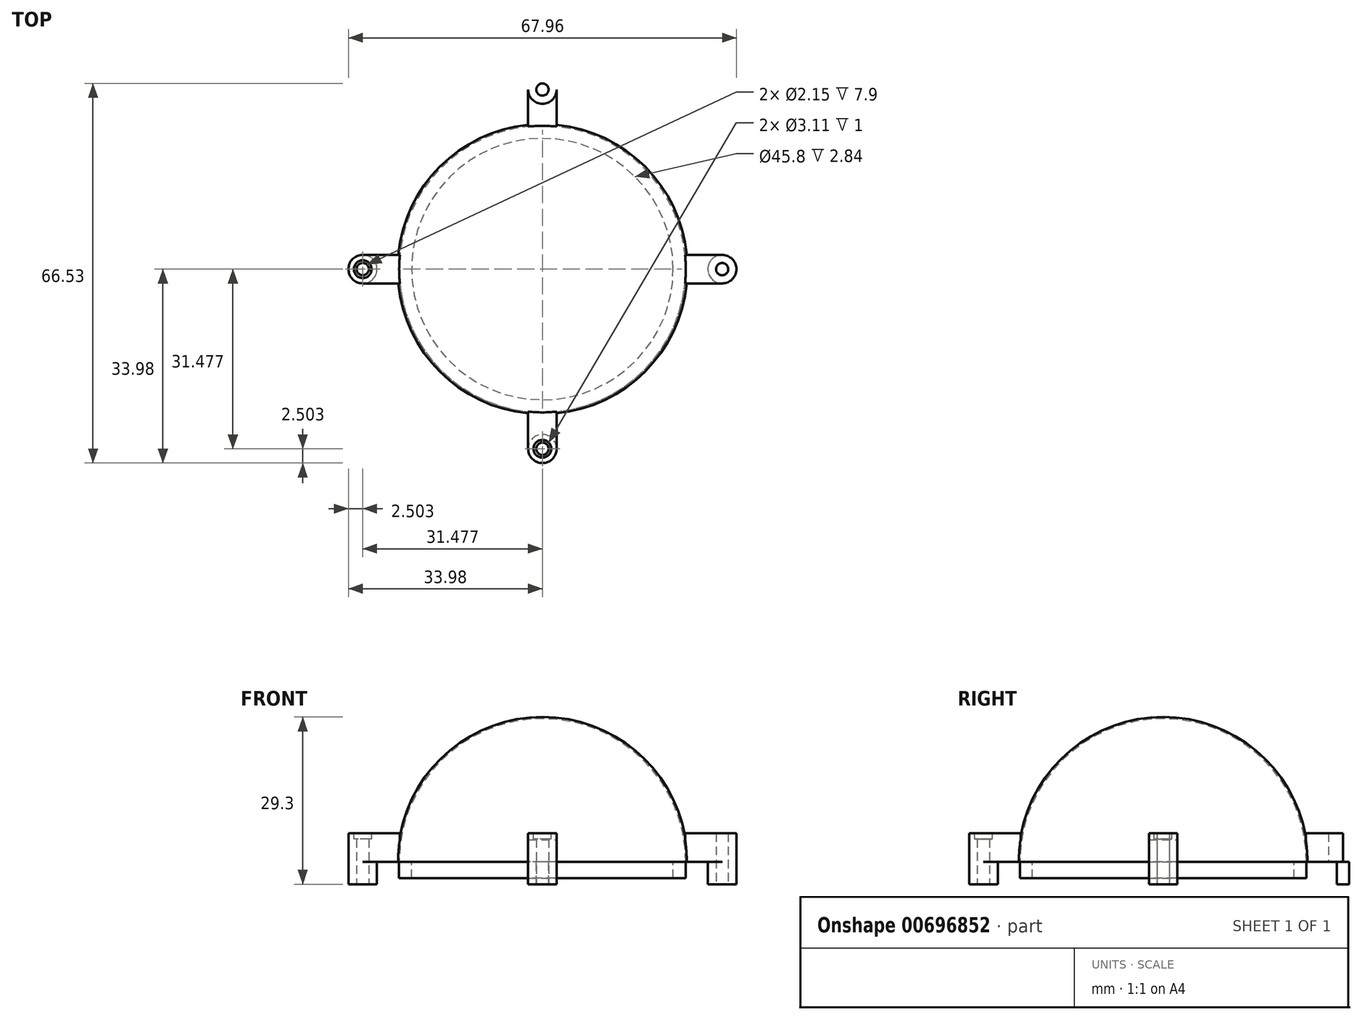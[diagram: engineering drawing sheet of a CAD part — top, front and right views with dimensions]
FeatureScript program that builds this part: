
annotation { "Feature Type Name" : "Feature", "Feature Type Description" : "" }
export const myFeature = defineFeature(function(context is Context, id is Id, definition is map)
    precondition{}
    {
        {
            var Q0;
            Q0=qCreatedBy(makeId("Top.planeOp"),FACE);
            var sketch = newSketch(context, id + "F0", { "sketchPlane" : qUnion([Q0])});
            skCircle(sketch, "E0", {"center": v(0, 0) * mm, "radius": 25.4 * mm});
            skCircle(sketch, "E1", {"center": v(0, 0) * mm, "radius": 22.9 * mm});
            skLineSegment(sketch, "E2", {"start": v(-75.08, 0) * mm, "end": v(76.97, 0) * mm});
            skLineSegment(sketch, "E3", {"start": v(-22.76, 2.5) * mm, "end": v(-31.48, 2.5) * mm});
            skLineSegment(sketch, "E4", {"start": v(-22.76, -2.5) * mm, "end": v(-31.48, -2.5) * mm});
            skCircle(sketch, "E5", {"center": v(-31.48, 0) * mm, "radius": 2.5 * mm});
            skPoint(sketch, "E6", {"position": v(-25.28, 2.5) * mm});
            skLineSegment(sketch, "E7.MirrorCS", {"start": v(22.76, 2.5) * mm, "end": v(31.48, 2.5) * mm});
            skLineSegment(sketch, "E8.MirrorCS", {"start": v(22.76, -2.5) * mm, "end": v(31.48, -2.5) * mm});
            skCircle(sketch, "E9.MirrorC", {"center": v(31.48, 0) * mm, "radius": 2.5 * mm});
            skLineSegment(sketch, "E10", {"start": v(0, 0) * mm, "end": v(95.02, -95.02) * mm, "construction": true});
            skLineSegment(sketch, "E11.MirrorCS", {"start": v(2.5, -22.76) * mm, "end": v(2.5, -31.48) * mm});
            skCircle(sketch, "E12.MirrorC", {"center": v(0, -31.48) * mm, "radius": 2.5 * mm});
            skLineSegment(sketch, "E13.MirrorCS", {"start": v(-2.5, -22.76) * mm, "end": v(-2.5, -31.48) * mm});
            skLineSegment(sketch, "E14.MirrorCS", {"start": v(2.5, 22.76) * mm, "end": v(2.5, 31.48) * mm});
            skCircle(sketch, "E15.MirrorC", {"center": v(0, 31.48) * mm, "radius": 2.5 * mm});
            skLineSegment(sketch, "E16.MirrorCS", {"start": v(-2.5, 22.76) * mm, "end": v(-2.5, 31.48) * mm});
            skCircle(sketch, "E17", {"center": v(0, -31.48) * mm, "radius": 1.07 * mm});
            skCircle(sketch, "E18.MirrorC", {"center": v(31.48, 0) * mm, "radius": 1.07 * mm});
            skCircle(sketch, "E19.MirrorC", {"center": v(0, 31.48) * mm, "radius": 1.07 * mm});
            skCircle(sketch, "E20.MirrorC", {"center": v(-31.48, 0) * mm, "radius": 1.07 * mm});
            skCircle(sketch, "E21", {"center": v(0, 0) * mm, "radius": 25.1 * mm});
            skCircle(sketch, "E22", {"center": v(0, 0) * mm, "radius": 2.5 * mm});
            skSolve(sketch);
        }
        {
            var Q0;
            {var subQ0=sQuery(id+"F0.wireOp",EDGE,"E7.MirrorCS");var subQ1=sQuery(id+"F0.wireOp",EDGE,"E0");var subQ2=makeQuery(id+"F0.imprint","INTERSECT",VERTEX,{"derivedFrom":[subQ1,subQ0]});Q0=makeQuery(id+"F0.imprint","IMPRINT",FACE,{"disambiguationData":[TD([[makeQuery(id+"F0.imprint","IMPRINT",EDGE,{"disambiguationData":[TD([[subQ2,-1.0]])],"derivedFrom":subQ1}),1.0]])]});}
            var Q1;
            {var subQ0=sQuery(id+"F0.wireOp",EDGE,"E7.MirrorCS");var subQ1=sQuery(id+"F0.wireOp",EDGE,"E0");var subQ2=makeQuery(id+"F0.imprint","INTERSECT",VERTEX,{"derivedFrom":[subQ1,subQ0]});Q1=makeQuery(id+"F0.imprint","IMPRINT",FACE,{"disambiguationData":[TD([[makeQuery(id+"F0.imprint","IMPRINT",EDGE,{"disambiguationData":[TD([[subQ2,1.0]])],"derivedFrom":subQ1}),1.0]])]});}
            var Q2;
            {var subQ0=sQuery(id+"F0.wireOp",EDGE,"E14.MirrorCS");var subQ1=sQuery(id+"F0.wireOp",EDGE,"E0");var subQ2=makeQuery(id+"F0.imprint","INTERSECT",VERTEX,{"derivedFrom":[subQ1,subQ0]});Q2=makeQuery(id+"F0.imprint","IMPRINT",FACE,{"disambiguationData":[TD([[makeQuery(id+"F0.imprint","IMPRINT",EDGE,{"disambiguationData":[TD([[subQ2,-1.0]])],"derivedFrom":subQ1}),1.0]])]});}
            var Q3;
            {var subQ0=sQuery(id+"F0.wireOp",EDGE,"E16.MirrorCS");var subQ1=sQuery(id+"F0.wireOp",EDGE,"E0");var subQ2=makeQuery(id+"F0.imprint","INTERSECT",VERTEX,{"derivedFrom":[subQ1,subQ0]});Q3=makeQuery(id+"F0.imprint","IMPRINT",FACE,{"disambiguationData":[TD([[makeQuery(id+"F0.imprint","IMPRINT",EDGE,{"disambiguationData":[TD([[subQ2,-1.0]])],"derivedFrom":subQ1}),1.0]])]});}
            var Q4;
            {var subQ0=sQuery(id+"F0.wireOp",EDGE,"E3");var subQ1=sQuery(id+"F0.wireOp",EDGE,"E0");var subQ2=makeQuery(id+"F0.imprint","INTERSECT",VERTEX,{"derivedFrom":[subQ1,subQ0]});Q4=makeQuery(id+"F0.imprint","IMPRINT",FACE,{"disambiguationData":[TD([[makeQuery(id+"F0.imprint","IMPRINT",EDGE,{"disambiguationData":[TD([[subQ2,-1.0]])],"derivedFrom":subQ1}),1.0]])]});}
            var Q5;
            Q5=sQuery(id+"F0.wireOp",EDGE,"E2");
            revolve(context, id + "F1", {"entities" : qUnion([Q0, Q1, Q2, Q3, Q4]), "axis" : qUnion([Q5]), "revolveType" : RevolveType.ONE_DIRECTION, "angle" : 180 * degree});
        }
        {
            var Q0;
            {var subQ0=sQuery(id+"F0.wireOp",EDGE,"E7.MirrorCS");var subQ1=sQuery(id+"F0.wireOp",EDGE,"E0");var subQ2=makeQuery(id+"F0.imprint","INTERSECT",VERTEX,{"derivedFrom":[subQ1,subQ0]});Q0=makeQuery(id+"F0.imprint","IMPRINT",FACE,{"disambiguationData":[TD([[makeQuery(id+"F0.imprint","IMPRINT",EDGE,{"disambiguationData":[TD([[subQ2,1.0]])],"derivedFrom":subQ1}),-1.0]])]});}
            var Q1;
            {var subQ0=sQuery(id+"F0.wireOp",EDGE,"E8.MirrorCS");var subQ1=sQuery(id+"F0.wireOp",EDGE,"E0");var subQ2=makeQuery(id+"F0.imprint","INTERSECT",VERTEX,{"derivedFrom":[subQ1,subQ0]});Q1=makeQuery(id+"F0.imprint","IMPRINT",FACE,{"disambiguationData":[TD([[makeQuery(id+"F0.imprint","IMPRINT",EDGE,{"disambiguationData":[TD([[subQ2,-1.0]])],"derivedFrom":subQ1}),-1.0]])]});}
            var Q2;
            {var subQ0=sQuery(id+"F0.wireOp",EDGE,"E9.MirrorC");var subQ1=sQuery(id+"F0.wireOp",EDGE,"E2");var subQ2=makeQuery(id+"F0.imprint","INTERSECT",VERTEX,{"disambiguationData":[OD(0.0)],"derivedFrom":[subQ1,subQ0]});Q2=makeQuery(id+"F0.imprint","IMPRINT",FACE,{"disambiguationData":[TD([[makeQuery(id+"F0.imprint","IMPRINT",EDGE,{"disambiguationData":[TD([[subQ2,1.0]])],"derivedFrom":subQ1}),1.0]])]});}
            var Q3;
            {var subQ0=sQuery(id+"F0.wireOp",EDGE,"E9.MirrorC");var subQ1=sQuery(id+"F0.wireOp",EDGE,"E2");var subQ2=makeQuery(id+"F0.imprint","INTERSECT",VERTEX,{"disambiguationData":[OD(0.0)],"derivedFrom":[subQ1,subQ0]});Q3=makeQuery(id+"F0.imprint","IMPRINT",FACE,{"disambiguationData":[TD([[makeQuery(id+"F0.imprint","IMPRINT",EDGE,{"disambiguationData":[TD([[subQ2,1.0]])],"derivedFrom":subQ1}),-1.0]])]});}
            var Q4;
            {var subQ0=sQuery(id+"F0.wireOp",EDGE,"E7.MirrorCS");var subQ1=sQuery(id+"F0.wireOp",EDGE,"E0");var subQ2=makeQuery(id+"F0.imprint","INTERSECT",VERTEX,{"derivedFrom":[subQ1,subQ0]});Q4=makeQuery(id+"F0.imprint","IMPRINT",FACE,{"disambiguationData":[TD([[makeQuery(id+"F0.imprint","IMPRINT",EDGE,{"disambiguationData":[TD([[subQ2,1.0]])],"derivedFrom":subQ1}),1.0]])]});}
            var Q5;
            {var subQ0=sQuery(id+"F0.wireOp",EDGE,"E8.MirrorCS");var subQ1=sQuery(id+"F0.wireOp",EDGE,"E0");var subQ2=makeQuery(id+"F0.imprint","INTERSECT",VERTEX,{"derivedFrom":[subQ1,subQ0]});Q5=makeQuery(id+"F0.imprint","IMPRINT",FACE,{"disambiguationData":[TD([[makeQuery(id+"F0.imprint","IMPRINT",EDGE,{"disambiguationData":[TD([[subQ2,-1.0]])],"derivedFrom":subQ1}),1.0]])]});}
            var Q6;
            {var subQ0=sQuery(id+"F0.wireOp",EDGE,"E14.MirrorCS");var subQ1=sQuery(id+"F0.wireOp",EDGE,"E0");var subQ2=makeQuery(id+"F0.imprint","INTERSECT",VERTEX,{"derivedFrom":[subQ1,subQ0]});Q6=makeQuery(id+"F0.imprint","IMPRINT",FACE,{"disambiguationData":[TD([[makeQuery(id+"F0.imprint","IMPRINT",EDGE,{"disambiguationData":[TD([[subQ2,-1.0]])],"derivedFrom":subQ1}),1.0]])]});}
            var Q7;
            {var subQ0=sQuery(id+"F0.wireOp",EDGE,"E14.MirrorCS");var subQ1=sQuery(id+"F0.wireOp",EDGE,"E0");var subQ2=makeQuery(id+"F0.imprint","INTERSECT",VERTEX,{"derivedFrom":[subQ1,subQ0]});Q7=makeQuery(id+"F0.imprint","IMPRINT",FACE,{"disambiguationData":[TD([[makeQuery(id+"F0.imprint","IMPRINT",EDGE,{"disambiguationData":[TD([[subQ2,-1.0]])],"derivedFrom":subQ1}),-1.0]])]});}
            var Q8;
            {var subQ0=sQuery(id+"F0.wireOp",EDGE,"E15.MirrorC");var subQ1=makeQuery(id+"F0.imprint","INTERSECT",VERTEX,{"derivedFrom":[sQuery(id+"F0.wireOp",EDGE,"E14.MirrorCS"),subQ0]});Q8=makeQuery(id+"F0.imprint","IMPRINT",FACE,{"disambiguationData":[TD([[makeQuery(id+"F0.imprint","IMPRINT",EDGE,{"disambiguationData":[TD([[subQ1,1.0]])],"derivedFrom":subQ0}),-1.0]])]});}
            var Q9;
            {var subQ0=sQuery(id+"F0.wireOp",EDGE,"E3");var subQ1=sQuery(id+"F0.wireOp",EDGE,"E0");var subQ2=makeQuery(id+"F0.imprint","INTERSECT",VERTEX,{"derivedFrom":[subQ1,subQ0]});Q9=makeQuery(id+"F0.imprint","IMPRINT",FACE,{"disambiguationData":[TD([[makeQuery(id+"F0.imprint","IMPRINT",EDGE,{"disambiguationData":[TD([[subQ2,-1.0]])],"derivedFrom":subQ1}),-1.0]])]});}
            var Q10;
            {var subQ0=sQuery(id+"F0.wireOp",EDGE,"E5");var subQ1=sQuery(id+"F0.wireOp",EDGE,"E2");var subQ2=makeQuery(id+"F0.imprint","INTERSECT",VERTEX,{"disambiguationData":[OD(0.0)],"derivedFrom":[subQ1,subQ0]});Q10=makeQuery(id+"F0.imprint","IMPRINT",FACE,{"disambiguationData":[TD([[makeQuery(id+"F0.imprint","IMPRINT",EDGE,{"disambiguationData":[TD([[subQ2,-1.0]])],"derivedFrom":subQ1}),1.0]])]});}
            var Q11;
            {var subQ0=sQuery(id+"F0.wireOp",EDGE,"E5");var subQ1=sQuery(id+"F0.wireOp",EDGE,"E2");var subQ2=makeQuery(id+"F0.imprint","INTERSECT",VERTEX,{"disambiguationData":[OD(0.0)],"derivedFrom":[subQ1,subQ0]});Q11=makeQuery(id+"F0.imprint","IMPRINT",FACE,{"disambiguationData":[TD([[makeQuery(id+"F0.imprint","IMPRINT",EDGE,{"disambiguationData":[TD([[subQ2,-1.0]])],"derivedFrom":subQ1}),-1.0]])]});}
            var Q12;
            {var subQ0=sQuery(id+"F0.wireOp",EDGE,"E4");var subQ1=sQuery(id+"F0.wireOp",EDGE,"E0");var subQ2=makeQuery(id+"F0.imprint","INTERSECT",VERTEX,{"derivedFrom":[subQ1,subQ0]});Q12=makeQuery(id+"F0.imprint","IMPRINT",FACE,{"disambiguationData":[TD([[makeQuery(id+"F0.imprint","IMPRINT",EDGE,{"disambiguationData":[TD([[subQ2,1.0]])],"derivedFrom":subQ1}),-1.0]])]});}
            var Q13;
            {var subQ0=sQuery(id+"F0.wireOp",EDGE,"E4");var subQ1=sQuery(id+"F0.wireOp",EDGE,"E0");var subQ2=makeQuery(id+"F0.imprint","INTERSECT",VERTEX,{"derivedFrom":[subQ1,subQ0]});Q13=makeQuery(id+"F0.imprint","IMPRINT",FACE,{"disambiguationData":[TD([[makeQuery(id+"F0.imprint","IMPRINT",EDGE,{"disambiguationData":[TD([[subQ2,1.0]])],"derivedFrom":subQ1}),1.0]])]});}
            var Q14;
            {var subQ0=sQuery(id+"F0.wireOp",EDGE,"E3");var subQ1=sQuery(id+"F0.wireOp",EDGE,"E0");var subQ2=makeQuery(id+"F0.imprint","INTERSECT",VERTEX,{"derivedFrom":[subQ1,subQ0]});Q14=makeQuery(id+"F0.imprint","IMPRINT",FACE,{"disambiguationData":[TD([[makeQuery(id+"F0.imprint","IMPRINT",EDGE,{"disambiguationData":[TD([[subQ2,-1.0]])],"derivedFrom":subQ1}),1.0]])]});}
            var Q15;
            {var subQ0=sQuery(id+"F0.wireOp",EDGE,"E12.MirrorC");var subQ1=makeQuery(id+"F0.imprint","INTERSECT",VERTEX,{"derivedFrom":[sQuery(id+"F0.wireOp",EDGE,"E11.MirrorCS"),subQ0]});Q15=makeQuery(id+"F0.imprint","IMPRINT",FACE,{"disambiguationData":[TD([[makeQuery(id+"F0.imprint","IMPRINT",EDGE,{"disambiguationData":[TD([[subQ1,1.0]])],"derivedFrom":subQ0}),1.0]])]});}
            var Q16;
            {var subQ0=sQuery(id+"F0.wireOp",EDGE,"E13.MirrorCS");var subQ1=sQuery(id+"F0.wireOp",EDGE,"E0");var subQ2=makeQuery(id+"F0.imprint","INTERSECT",VERTEX,{"derivedFrom":[subQ1,subQ0]});Q16=makeQuery(id+"F0.imprint","IMPRINT",FACE,{"disambiguationData":[TD([[makeQuery(id+"F0.imprint","IMPRINT",EDGE,{"disambiguationData":[TD([[subQ2,-1.0]])],"derivedFrom":subQ1}),-1.0]])]});}
            var Q17;
            {var subQ0=sQuery(id+"F0.wireOp",EDGE,"E13.MirrorCS");var subQ1=sQuery(id+"F0.wireOp",EDGE,"E0");var subQ2=makeQuery(id+"F0.imprint","INTERSECT",VERTEX,{"derivedFrom":[subQ1,subQ0]});Q17=makeQuery(id+"F0.imprint","IMPRINT",FACE,{"disambiguationData":[TD([[makeQuery(id+"F0.imprint","IMPRINT",EDGE,{"disambiguationData":[TD([[subQ2,-1.0]])],"derivedFrom":subQ1}),1.0]])]});}
            extrude(context, id + "F2", {"entities" : qUnion([Q0, Q1, Q2, Q3, Q4, Q5, Q6, Q7, Q8, Q9, Q10, Q11, Q12, Q13, Q14, Q15, Q16, Q17]), "depth" : 5 * mm, "offsetDistance" : 25 * mm});
        }
        {
            var Q0;
            {var subQ0=sQuery(id+"F0.wireOp",EDGE,"E7.MirrorCS");var subQ1=sQuery(id+"F0.wireOp",EDGE,"E1");var subQ2=makeQuery(id+"F0.imprint","INTERSECT",VERTEX,{"derivedFrom":[subQ1,subQ0]});Q0=makeQuery(id+"F0.imprint","IMPRINT",FACE,{"disambiguationData":[TD([[makeQuery(id+"F0.imprint","IMPRINT",EDGE,{"disambiguationData":[TD([[subQ2,-1.0]])],"derivedFrom":subQ1}),-1.0]])]});}
            var Q1;
            {var subQ0=sQuery(id+"F0.wireOp",EDGE,"E7.MirrorCS");var subQ1=sQuery(id+"F0.wireOp",EDGE,"E1");var subQ2=makeQuery(id+"F0.imprint","INTERSECT",VERTEX,{"derivedFrom":[subQ1,subQ0]});Q1=makeQuery(id+"F0.imprint","IMPRINT",FACE,{"disambiguationData":[TD([[makeQuery(id+"F0.imprint","IMPRINT",EDGE,{"disambiguationData":[TD([[subQ2,1.0]])],"derivedFrom":subQ1}),-1.0]])]});}
            var Q2;
            {var subQ0=sQuery(id+"F0.wireOp",EDGE,"E8.MirrorCS");var subQ1=sQuery(id+"F0.wireOp",EDGE,"E1");var subQ2=makeQuery(id+"F0.imprint","INTERSECT",VERTEX,{"derivedFrom":[subQ1,subQ0]});Q2=makeQuery(id+"F0.imprint","IMPRINT",FACE,{"disambiguationData":[TD([[makeQuery(id+"F0.imprint","IMPRINT",EDGE,{"disambiguationData":[TD([[subQ2,-1.0]])],"derivedFrom":subQ1}),-1.0]])]});}
            var Q3;
            {var subQ0=sQuery(id+"F0.wireOp",EDGE,"E8.MirrorCS");var subQ1=sQuery(id+"F0.wireOp",EDGE,"E1");var subQ2=makeQuery(id+"F0.imprint","INTERSECT",VERTEX,{"derivedFrom":[subQ1,subQ0]});Q3=makeQuery(id+"F0.imprint","IMPRINT",FACE,{"disambiguationData":[TD([[makeQuery(id+"F0.imprint","IMPRINT",EDGE,{"disambiguationData":[TD([[subQ2,1.0]])],"derivedFrom":subQ1}),-1.0]])]});}
            var Q4;
            {var subQ0=sQuery(id+"F0.wireOp",EDGE,"E11.MirrorCS");var subQ1=sQuery(id+"F0.wireOp",EDGE,"E1");var subQ2=makeQuery(id+"F0.imprint","INTERSECT",VERTEX,{"derivedFrom":[subQ1,subQ0]});Q4=makeQuery(id+"F0.imprint","IMPRINT",FACE,{"disambiguationData":[TD([[makeQuery(id+"F0.imprint","IMPRINT",EDGE,{"disambiguationData":[TD([[subQ2,1.0]])],"derivedFrom":subQ1}),-1.0]])]});}
            var Q5;
            {var subQ0=sQuery(id+"F0.wireOp",EDGE,"E4");var subQ1=sQuery(id+"F0.wireOp",EDGE,"E1");var subQ2=makeQuery(id+"F0.imprint","INTERSECT",VERTEX,{"derivedFrom":[subQ1,subQ0]});Q5=makeQuery(id+"F0.imprint","IMPRINT",FACE,{"disambiguationData":[TD([[makeQuery(id+"F0.imprint","IMPRINT",EDGE,{"disambiguationData":[TD([[subQ2,-1.0]])],"derivedFrom":subQ1}),-1.0]])]});}
            var Q6;
            {var subQ0=sQuery(id+"F0.wireOp",EDGE,"E4");var subQ1=sQuery(id+"F0.wireOp",EDGE,"E1");var subQ2=makeQuery(id+"F0.imprint","INTERSECT",VERTEX,{"derivedFrom":[subQ1,subQ0]});Q6=makeQuery(id+"F0.imprint","IMPRINT",FACE,{"disambiguationData":[TD([[makeQuery(id+"F0.imprint","IMPRINT",EDGE,{"disambiguationData":[TD([[subQ2,1.0]])],"derivedFrom":subQ1}),-1.0]])]});}
            var Q7;
            {var subQ0=sQuery(id+"F0.wireOp",EDGE,"E3");var subQ1=sQuery(id+"F0.wireOp",EDGE,"E1");var subQ2=makeQuery(id+"F0.imprint","INTERSECT",VERTEX,{"derivedFrom":[subQ1,subQ0]});Q7=makeQuery(id+"F0.imprint","IMPRINT",FACE,{"disambiguationData":[TD([[makeQuery(id+"F0.imprint","IMPRINT",EDGE,{"disambiguationData":[TD([[subQ2,-1.0]])],"derivedFrom":subQ1}),-1.0]])]});}
            var Q8;
            {var subQ0=sQuery(id+"F0.wireOp",EDGE,"E3");var subQ1=sQuery(id+"F0.wireOp",EDGE,"E1");var subQ2=makeQuery(id+"F0.imprint","INTERSECT",VERTEX,{"derivedFrom":[subQ1,subQ0]});Q8=makeQuery(id+"F0.imprint","IMPRINT",FACE,{"disambiguationData":[TD([[makeQuery(id+"F0.imprint","IMPRINT",EDGE,{"disambiguationData":[TD([[subQ2,1.0]])],"derivedFrom":subQ1}),-1.0]])]});}
            var Q9;
            {var subQ0=sQuery(id+"F0.wireOp",EDGE,"E14.MirrorCS");var subQ1=sQuery(id+"F0.wireOp",EDGE,"E1");var subQ2=makeQuery(id+"F0.imprint","INTERSECT",VERTEX,{"derivedFrom":[subQ1,subQ0]});Q9=makeQuery(id+"F0.imprint","IMPRINT",FACE,{"disambiguationData":[TD([[makeQuery(id+"F0.imprint","IMPRINT",EDGE,{"disambiguationData":[TD([[subQ2,-1.0]])],"derivedFrom":subQ1}),-1.0]])]});}
            extrude(context, id + "F3", {"entities" : qUnion([Q0, Q1, Q2, Q3, Q4, Q5, Q6, Q7, Q8, Q9]), "operationType" : NewBodyOperationType.ADD, "oppositeDirection" : true, "depth" : 2.84 * mm, "offsetDistance" : 25 * mm});
        }
        {
            var Q0;
            {var subQ0=sQuery(id+"F0.wireOp",EDGE,"E5");var subQ2=sQuery(id+"F0.wireOp",EDGE,"E2");var subQ6=makeQuery(id+"F0.imprint","INTERSECT",VERTEX,{"disambiguationData":[OD(0.0)],"derivedFrom":[subQ2,subQ0]});Q0=makeQuery(id+"F0.imprint","IMPRINT",FACE,{"disambiguationData":[TD([[makeQuery(id+"F0.imprint","IMPRINT",EDGE,{"disambiguationData":[TD([[subQ6,-1.0]])],"derivedFrom":subQ2}),1.0]])]});}
            var Q1;
            {var subQ0=sQuery(id+"F0.wireOp",EDGE,"E5");var subQ2=sQuery(id+"F0.wireOp",EDGE,"E2");var subQ3=makeQuery(id+"F0.imprint","INTERSECT",VERTEX,{"disambiguationData":[OD(0.0)],"derivedFrom":[subQ2,subQ0]});Q1=makeQuery(id+"F0.imprint","IMPRINT",FACE,{"disambiguationData":[TD([[makeQuery(id+"F0.imprint","IMPRINT",EDGE,{"disambiguationData":[TD([[subQ3,-1.0]])],"derivedFrom":subQ2}),-1.0]])]});}
            var Q2;
            Q2=makeQuery(id+"F0.imprint","IMPRINT",FACE,{"disambiguationData":[TD([[makeQuery(id+"F0.imprint","IMPRINT",EDGE,{"derivedFrom":sQuery(id+"F0.wireOp",EDGE,"E17")}),-1.0]])]});
            var Q3;
            Q3=makeQuery(id+"F0.imprint","IMPRINT",FACE,{"disambiguationData":[TD([[makeQuery(id+"F0.imprint","IMPRINT",EDGE,{"derivedFrom":sQuery(id+"F0.wireOp",EDGE,"E19.MirrorC")}),1.0]])]});
            var Q4;
            {var subQ0=sQuery(id+"F0.wireOp",EDGE,"E9.MirrorC");var subQ2=sQuery(id+"F0.wireOp",EDGE,"E2");var subQ3=makeQuery(id+"F0.imprint","INTERSECT",VERTEX,{"disambiguationData":[OD(1.0)],"derivedFrom":[subQ2,subQ0]});Q4=makeQuery(id+"F0.imprint","IMPRINT",FACE,{"disambiguationData":[TD([[makeQuery(id+"F0.imprint","IMPRINT",EDGE,{"disambiguationData":[TD([[subQ3,-1.0]])],"derivedFrom":subQ2}),1.0]])]});}
            var Q5;
            {var subQ0=sQuery(id+"F0.wireOp",EDGE,"E9.MirrorC");var subQ2=sQuery(id+"F0.wireOp",EDGE,"E2");var subQ4=makeQuery(id+"F0.imprint","INTERSECT",VERTEX,{"disambiguationData":[OD(1.0)],"derivedFrom":[subQ2,subQ0]});Q5=makeQuery(id+"F0.imprint","IMPRINT",FACE,{"disambiguationData":[TD([[makeQuery(id+"F0.imprint","IMPRINT",EDGE,{"disambiguationData":[TD([[subQ4,-1.0]])],"derivedFrom":subQ2}),-1.0]])]});}
            extrude(context, id + "F4", {"entities" : qUnion([Q0, Q1, Q2, Q3, Q4, Q5]), "operationType" : NewBodyOperationType.ADD, "oppositeDirection" : true, "depth" : 3.9 * mm, "offsetDistance" : 25 * mm});
        }
        {
            var Q0;
            Q0=makeQuery(id+"F2.opExtrude","CAP_FACE",FACE,{"disambiguationData":[OSD([sQuery(id+"F0.wireOp",EDGE,"E3"),sQuery(id+"F0.wireOp",EDGE,"E4"),sQuery(id+"F0.wireOp",EDGE,"E5"),sQuery(id+"F0.wireOp",EDGE,"E20.MirrorC"),sQuery(id+"F0.wireOp",EDGE,"E21")])],"isStart":false});
            var sketch = newSketch(context, id + "F5", { "sketchPlane" : qUnion([Q0])});
            skCircle(sketch, "E23", {"center": v(-31.48, 0) * mm, "radius": 1.55 * mm});
            skCircle(sketch, "E24.MirrorC", {"center": v(31.48, 0) * mm, "radius": 1.55 * mm});
            skCircle(sketch, "E25.MirrorC", {"center": v(0, -31.48) * mm, "radius": 1.55 * mm});
            skCircle(sketch, "E26.MirrorC", {"center": v(0, 31.48) * mm, "radius": 1.55 * mm});
            skSolve(sketch);
        }
        {
            var Q0;
            Q0=makeQuery(id+"F5.imprint","IMPRINT",FACE,{"disambiguationData":[TD([[makeQuery(id+"F5.imprint","IMPRINT",EDGE,{"derivedFrom":sQuery(id+"F5.wireOp",EDGE,"E25.MirrorC")}),1.0]])]});
            var Q1;
            Q1=makeQuery(id+"F5.imprint","IMPRINT",FACE,{"disambiguationData":[TD([[makeQuery(id+"F5.imprint","IMPRINT",EDGE,{"derivedFrom":sQuery(id+"F5.wireOp",EDGE,"E23")}),1.0]])]});
            var Q2;
            Q2=makeQuery(id+"F5.imprint","IMPRINT",FACE,{"disambiguationData":[TD([[makeQuery(id+"F5.imprint","IMPRINT",EDGE,{"derivedFrom":sQuery(id+"F5.wireOp",EDGE,"E26.MirrorC")}),-1.0]])]});
            var Q3;
            Q3=makeQuery(id+"F5.imprint","IMPRINT",FACE,{"disambiguationData":[TD([[makeQuery(id+"F5.imprint","IMPRINT",EDGE,{"derivedFrom":sQuery(id+"F5.wireOp",EDGE,"E24.MirrorC")}),-1.0]])]});
            extrude(context, id + "F6", {"entities" : qUnion([Q0, Q1, Q2, Q3]), "operationType" : NewBodyOperationType.REMOVE, "oppositeDirection" : true, "depth" : 1 * mm, "offsetDistance" : 25 * mm});
        }
    });
